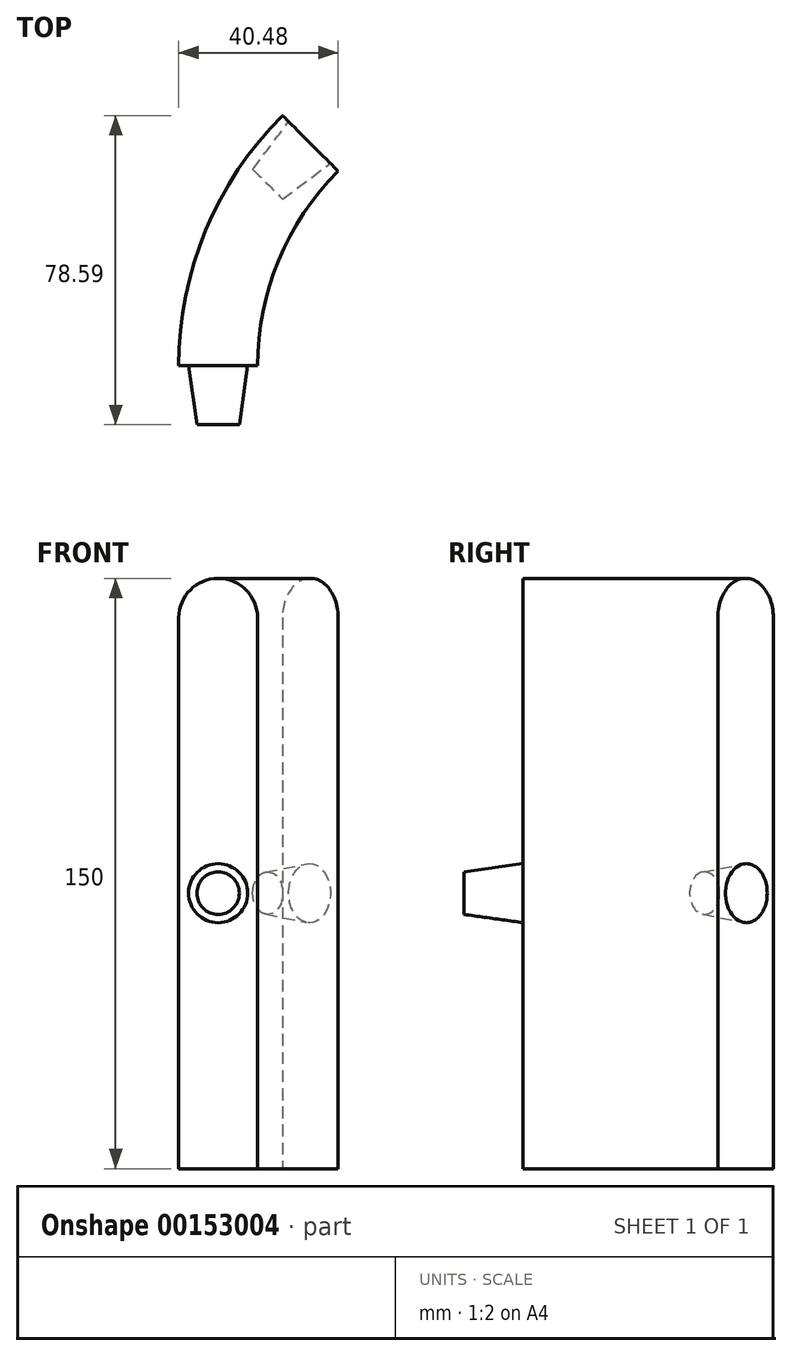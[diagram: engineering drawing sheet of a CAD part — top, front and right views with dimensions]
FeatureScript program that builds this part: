
annotation { "Feature Type Name" : "Feature", "Feature Type Description" : "" }
export const myFeature = defineFeature(function(context is Context, id is Id, definition is map)
    precondition{}
    {
        {
            var Q0;
            Q0=qCreatedBy(makeId("Front.planeOp"),FACE);
            var sketch = newSketch(context, id + "F0", { "sketchPlane" : qUnion([Q0])});
            skLineSegment(sketch, "E0", {"start": v(127.32, 299.12) * mm, "end": v(127.32, 149.12) * mm});
            skLineSegment(sketch, "E1", {"start": v(127.32, 299.12) * mm, "end": v(37.4, 299.12) * mm});
            skLineSegment(sketch, "E2", {"start": v(37.4, 299.12) * mm, "end": v(37.4, 149.12) * mm});
            skLineSegment(sketch, "E3", {"start": v(37.4, 149.12) * mm, "end": v(127.32, 149.12) * mm});
            skSolve(sketch);
        }
        {
            var Q0;
            Q0=makeQuery(id+"F0.imprint","IMPRINT",FACE,{"disambiguationData":[TD([[makeQuery(id+"F0.imprint","IMPRINT",EDGE,{"derivedFrom":sQuery(id+"F0.wireOp",EDGE,"qIKZoeJY-TQep-c7Ri-jmz6-qnDqXJ4BGPkj")}),1.0]])]});
            var Q1;
            Q1=makeQuery(id+"F0.imprint","IMPRINT",FACE,{"disambiguationData":[TD([[makeQuery(id+"F0.imprint","IMPRINT",EDGE,{"derivedFrom":sQuery(id+"F0.wireOp",EDGE,"E0")}),-1.0]])]});
            var Q2;
            Q2=sQuery(id+"F0.wireOp",EDGE,"E0");
            revolve(context, id + "F1", {"entities" : qUnion([Q0, Q1]), "axis" : qUnion([Q2]), "revolveType" : RevolveType.ONE_DIRECTION, "angle" : 45 * degree});
        }
        {
            var Q0;
            Q0=makeQuery(id+"F1.opRevolve","CAP_FACE",FACE,{"disambiguationData":[OSD([sQuery(id+"F0.wireOp",EDGE,"c1a47f16-03cb-4326-a7fb-4da27e49267e"),sQuery(id+"F0.wireOp",EDGE,"0445b6aa-1599-4f51-a42e-cd0f4c540e00"),sQuery(id+"F0.wireOp",EDGE,"2b562399-184e-4d8c-bb95-a8394558efe5.trimOffspring"),sQuery(id+"F0.wireOp",EDGE,"qIKZoeJY-TQep-c7Ri-jmz6-qnDqXJ4BGPkj"),sQuery(id+"F0.wireOp",EDGE,"5GoxPhpb-W2qU-YVQz-mgj7-7G05RjJSTRpR"),sQuery(id+"F0.wireOp",EDGE,"W7TmGzvV-SRVJ-wapx-RxKG-6s7Lfqn86I50"),sQuery(id+"F0.wireOp",EDGE,"FrPlEDyA-e7Am-JMK7-J0is-8kwWFS23w3qv")])],"isStart":false});
            var Q1;
            Q1=makeQuery(id+"F1.opRevolve","CAP_FACE",FACE,{"disambiguationData":[OSD([sQuery(id+"F0.wireOp",EDGE,"c1a47f16-03cb-4326-a7fb-4da27e49267e"),sQuery(id+"F0.wireOp",EDGE,"0445b6aa-1599-4f51-a42e-cd0f4c540e00"),sQuery(id+"F0.wireOp",EDGE,"2b562399-184e-4d8c-bb95-a8394558efe5.trimOffspring"),sQuery(id+"F0.wireOp",EDGE,"qIKZoeJY-TQep-c7Ri-jmz6-qnDqXJ4BGPkj"),sQuery(id+"F0.wireOp",EDGE,"5GoxPhpb-W2qU-YVQz-mgj7-7G05RjJSTRpR"),sQuery(id+"F0.wireOp",EDGE,"W7TmGzvV-SRVJ-wapx-RxKG-6s7Lfqn86I50"),sQuery(id+"F0.wireOp",EDGE,"FrPlEDyA-e7Am-JMK7-J0is-8kwWFS23w3qv")])],"isStart":true});
            var Q2;
            Q2=makeQuery(id+"F1.opRevolve","SWEPT_FACE",FACE,{"disambiguationData":[OSD([sQuery(id+"F0.wireOp",EDGE,"qIKZoeJY-TQep-c7Ri-jmz6-qnDqXJ4BGPkj")])]});
            var Q3;
            Q3=makeQuery(id+"F1.opRevolve","SWEPT_FACE",FACE,{"disambiguationData":[OSD([sQuery(id+"F0.wireOp",EDGE,"FrPlEDyA-e7Am-JMK7-J0is-8kwWFS23w3qv")])]});
            var Q4;
            Q4=makeQuery(id+"F1.opRevolve","SWEPT_FACE",FACE,{"disambiguationData":[OSD([sQuery(id+"F0.wireOp",EDGE,"Zfw3s35M-H7I7-ctV8-WwCO-TXvZiI164tsA")])]});
            var Q5;
            Q5=makeQuery(id+"F1.opRevolve","SWEPT_FACE",FACE,{"disambiguationData":[OSD([sQuery(id+"F0.wireOp",EDGE,"DxNpelhW-NPha-Za65-5rby-Dc9gSIxmAqf3")])]});
            var Q6;
            Q6=makeQuery(id+"F1.opRevolve","CAP_FACE",FACE,{"disambiguationData":[OSD([sQuery(id+"F0.wireOp",EDGE,"E0"),sQuery(id+"F0.wireOp",EDGE,"h8w9ds9V-v6di-2uzp-dC4j-q0jaSeQ5vev1"),sQuery(id+"F0.wireOp",EDGE,"rqYKbdp3-fYyZ-YRGA-wxHp-ysZJsVzrtoBV"),sQuery(id+"F0.wireOp",EDGE,"CGmn5kAD-aOFs-twpu-ufA2-BfELl45xMEkJ")])],"isStart":true});
            var Q7;
            Q7=makeQuery(id+"F1.opRevolve","CAP_FACE",FACE,{"disambiguationData":[OSD([sQuery(id+"F0.wireOp",EDGE,"E0"),sQuery(id+"F0.wireOp",EDGE,"h8w9ds9V-v6di-2uzp-dC4j-q0jaSeQ5vev1"),sQuery(id+"F0.wireOp",EDGE,"rqYKbdp3-fYyZ-YRGA-wxHp-ysZJsVzrtoBV"),sQuery(id+"F0.wireOp",EDGE,"CGmn5kAD-aOFs-twpu-ufA2-BfELl45xMEkJ")])],"isStart":false});
            var Q8;
            Q8=makeQuery(id+"F1.opRevolve","SWEPT_FACE",FACE,{"disambiguationData":[OSD([sQuery(id+"F0.wireOp",EDGE,"CGmn5kAD-aOFs-twpu-ufA2-BfELl45xMEkJ")])]});
            var Q9;
            Q9=makeQuery(id+"F1.opRevolve","SWEPT_FACE",FACE,{"disambiguationData":[OSD([sQuery(id+"F0.wireOp",EDGE,"rqYKbdp3-fYyZ-YRGA-wxHp-ysZJsVzrtoBV")])]});
            var Q10;
            Q10=makeQuery(id+"F1.opRevolve","SWEPT_FACE",FACE,{"disambiguationData":[OSD([sQuery(id+"F0.wireOp",EDGE,"E3")])]});
            var Q11;
            Q11=makeQuery(id+"F1.opRevolve","SWEPT_FACE",FACE,{"disambiguationData":[OSD([sQuery(id+"F0.wireOp",EDGE,"E1")])]});
            shell(context, id + "F2", {"entities" : qUnion([Q0, Q1, Q2, Q3, Q4, Q5, Q6, Q7, Q8, Q9, Q10, Q11]), "thickness" : 20 * mm});
        }
        {
            var Q0;
            Q0=makeQuery(id+"F1.opRevolve","CAP_FACE",FACE,{"disambiguationData":[OSD([sQuery(id+"F0.wireOp",EDGE,"E0"),sQuery(id+"F0.wireOp",EDGE,"h8w9ds9V-v6di-2uzp-dC4j-q0jaSeQ5vev1"),sQuery(id+"F0.wireOp",EDGE,"rqYKbdp3-fYyZ-YRGA-wxHp-ysZJsVzrtoBV"),sQuery(id+"F0.wireOp",EDGE,"CGmn5kAD-aOFs-twpu-ufA2-BfELl45xMEkJ")])],"isStart":true});
            var sketch = newSketch(context, id + "F3", { "sketchPlane" : qUnion([Q0])});
            skCircle(sketch, "E4", {"center": v(47.4, 219.12) * mm, "radius": 7.5 * mm});
            skSolve(sketch);
        }
        {
            var Q0;
            Q0=qSketchRegion(id+"F3",true);
            extrude(context, id + "F4", {"entities" : qUnion([Q0]), "operationType" : NewBodyOperationType.ADD, "depth" : 15 * mm, "hasDraft" : true, "draftAngle" : 8 * degree, "draftPullDirection" : true});
        }
        {
            var Q0;
            Q0=makeQuery(id+"F1.opRevolve","CAP_FACE",FACE,{"disambiguationData":[OSD([sQuery(id+"F0.wireOp",EDGE,"E0"),sQuery(id+"F0.wireOp",EDGE,"h8w9ds9V-v6di-2uzp-dC4j-q0jaSeQ5vev1"),sQuery(id+"F0.wireOp",EDGE,"rqYKbdp3-fYyZ-YRGA-wxHp-ysZJsVzrtoBV"),sQuery(id+"F0.wireOp",EDGE,"CGmn5kAD-aOFs-twpu-ufA2-BfELl45xMEkJ")])],"isStart":false});
            var sketch = newSketch(context, id + "F5", { "sketchPlane" : qUnion([Q0])});
            skCircle(sketch, "E5", {"center": v(-9.82, 219.12) * mm, "radius": 7.5 * mm});
            skSolve(sketch);
        }
        {
            var Q0;
            Q0=qSketchRegion(id+"F5",true);
            extrude(context, id + "F6", {"entities" : qUnion([Q0]), "operationType" : NewBodyOperationType.REMOVE, "oppositeDirection" : true, "depth" : 15 * mm, "hasDraft" : true, "draftAngle" : 8 * degree, "draftPullDirection" : true});
        }
        {
            var Q0;
            Q0=makeQuery(id+"F1.opRevolve","SWEPT_EDGE",EDGE,{"disambiguationData":[OSD([sQuery(id+"F0.wireOp",EDGE,"E1"),sQuery(id+"F0.wireOp",EDGE,"E2")])]});
            var Q1;
            Q1=makeQuery(id+"F2.opShell","OFFSET_EDGE",EDGE,{"disambiguationData":[OSD([sQuery(id+"F0.wireOp",EDGE,"E1"),sQuery(id+"F0.wireOp",EDGE,"E2")])]});
            fillet(context, id + "F7", {"entities" : qUnion([Q0, Q1]), "radius" : 10 * mm, "tangentPropagation" : true, "allowEdgeOverflow" : false});
        }
    });
